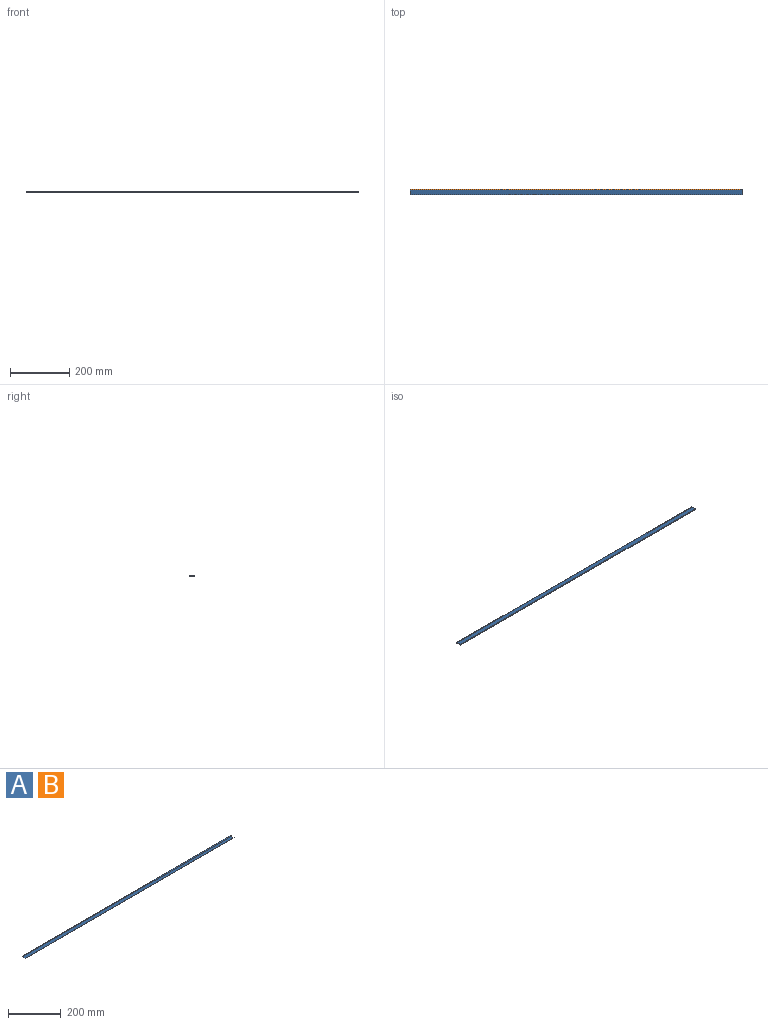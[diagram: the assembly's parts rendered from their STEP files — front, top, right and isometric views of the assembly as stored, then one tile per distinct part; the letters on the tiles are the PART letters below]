
ASSEMBLY  parts=2 mates=1
PART A: 6 faces, bbox 1120x17.6x3.2 mm
  f0: plane 1120x14.68mm, normal (0,0,1), area 16438.4mm2, adj f1,f3,f4,f5
  f1: plane 1120x0.7mm, normal (0,-1,0), area 784mm2, adj f0,f2,f4,f5
  f2: plane 1120x16mm, normal (0,0,-1), area 17920mm2, adj f1,f3,f4,f5
  f3: cylinder r=1.6mm len=1120mm, axis (-1,0,0), area 9515.2mm2, adj f0,f2,f4,f5
  f4: plane 17.6x3.2mm, normal (1,0,0), area 18.6mm2, adj f0,f1,f2,f3
  f5: plane 17.6x3.2mm, normal (-1,0,0), area 18.6mm2, adj f0,f1,f2,f3
PART B: same geometry as A
PLACE A rot(axis=(0,-1,0),180deg) t=(0,0,1031.2)mm
PLACE B at identity fixed
MATE revolute A.f3 <-> B.f3  axis (1,0,0) through (560,-1375,515.6)mm
